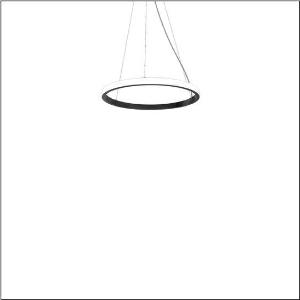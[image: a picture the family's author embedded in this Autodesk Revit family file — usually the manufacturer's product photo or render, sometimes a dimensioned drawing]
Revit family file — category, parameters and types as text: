
# Revit family: silica_r__21_ring-o_5pjbo1d1104a_1dcd
name_source: partatom
category: Lighting Fixtures
units: mm (PartAtom-declared; Revit-internal decimal feet)

## family parameters
Cut with Voids When Loaded = No
Host = Face
Light Source = No
Part Type = Normal
Room Calculation Point = No
Round Connector Dimension = Use Diameter
Shared = No

## types (1)
- Silica® 21 Ring-O (1 x LED, 3740 lm, 60 W, 3000K)
    Apparent Load = 60 VA
    CIE Flux Codes = 2 16 49 50 100
    Color Rendering = 80
    Color Temperature = 3000K
    Default Elevation = 1800 mm
    Description = Silica® 21 Ring-O, suspended luminaire, of PMMA, frosted, light emission: outer ring side luminous distribution, primary light characteristic: symmetric, installation type: suspended mounting, LED, rated luminous flux: 3.744lm, luminous efficacy: 62lm/W, light colour: 830, colour temperature: 3000K, with terminal, 5-pole, mains connection: 230V, AC/DC, 0/50..60Hz, rated input power: 60W, housing, of extruded aluminium section, jet black (RAL 9005), diameter: 610mm, ceiling canopy, jet black (RAL 9005), protection rating (lamp compartment): IP40, insulation class (complete): insulation class I (protective earthing), certification: CE, impact resistance: IK02, permissible operating ambient temperature: 0..+35°C, packaging unit: 1 piece
    Height = 48 mm  [stored 0.15748 ft]
    Lamp = 1 x LED
    Lamp Light Flux = 3740 lm
    Lamp Power = 60 W
    Lamp count = 1
    Length = 610 mm
    Luminous efficacy = 62 lm/W
    Manufacturer = Siteco
    ModVariant = No
    Model = 5PJBO1D1104A
    Mounting Place = Ceiling
    Mounting Type = Pendant
    Number of Poles = 1
    OnlyDefault = Yes
    Power Factor = 1
    Product Name = Silica® 21 Ring-O
    Product group = suspended luminaire
    ProductGroupID = 904
    Protection Class = Protection class I
    Protection Degree = Degree of protection
    RLX_Detail_Level = 1
    RLX_Emergency_Light_Flux = 0 lm
    RLX_Emergency_Type = 0
    RLX_Emergency_Type_DB = No
    RlxData = <blob elided: 12137 chars, md5=09870683>
    Socket = socket
    Standby Power = 0 W
    System Light Flux = 3740 lm
    System Power = 60 W
    Type Comments = Product without accessories
    Type Image = l_1258377.jpg
    URL = http://relux.com
    VarID = ---
    Voltage = 0 V
    Weight = 0.00 kg
    Width = 0 mm  [stored 0 ft]

note: [stored X ft] marks values corroborated as IEEE doubles in the binary element streams (Revit-internal decimal feet)

## geometry (parser evidence)
native form markers: Sweep x13
no freeform markers — native parametric forms only
